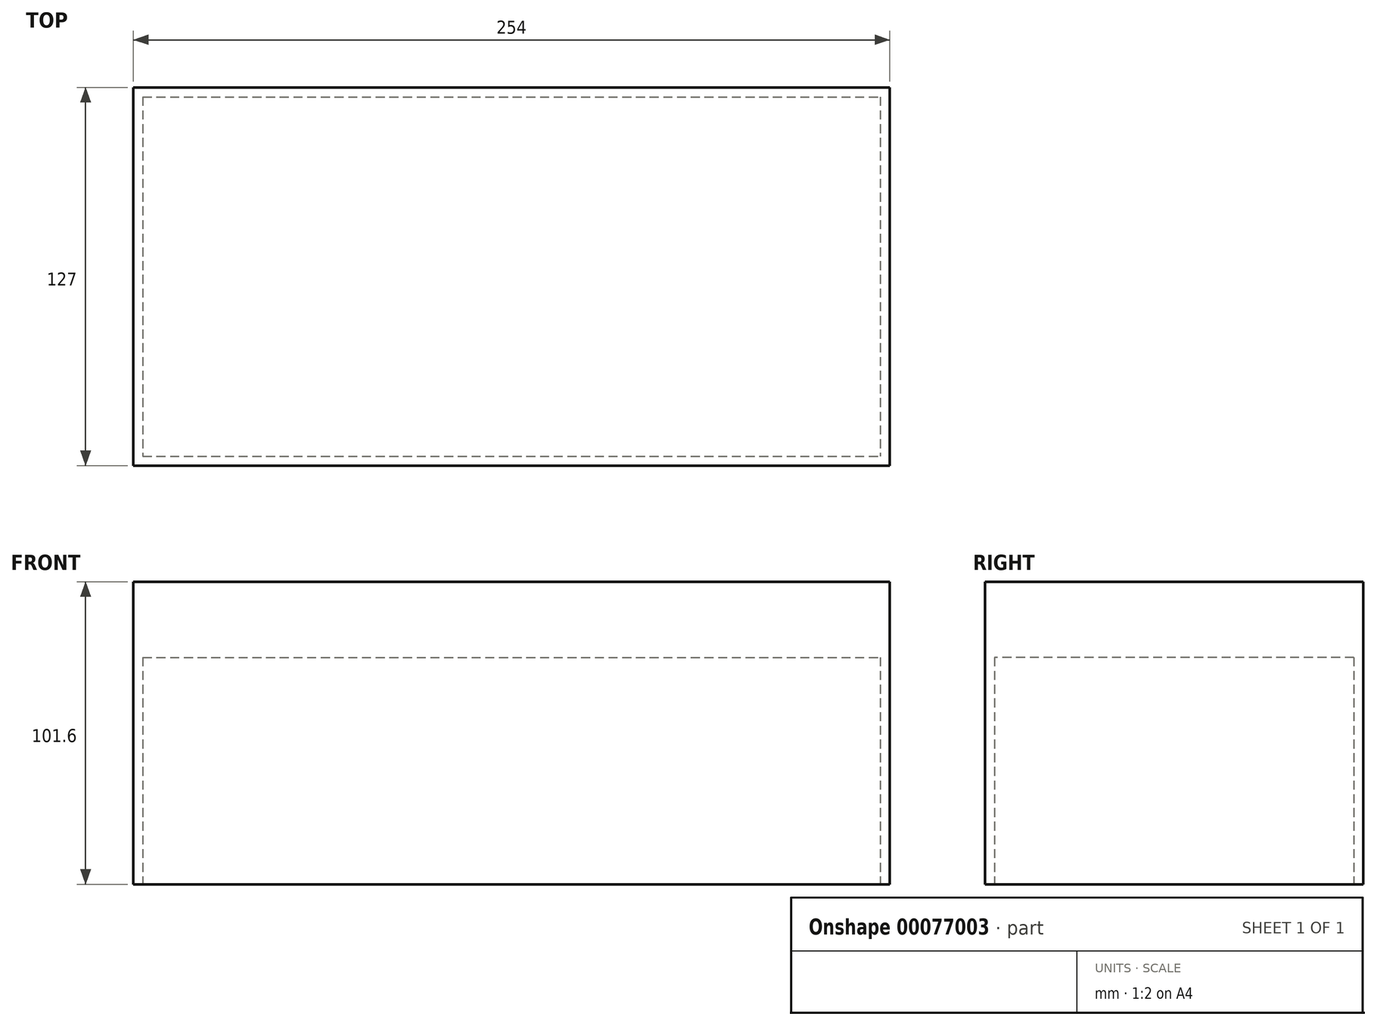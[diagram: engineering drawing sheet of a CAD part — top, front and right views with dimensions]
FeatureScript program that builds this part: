
annotation { "Feature Type Name" : "Feature", "Feature Type Description" : "" }
export const myFeature = defineFeature(function(context is Context, id is Id, definition is map)
    precondition{}
    {
        {
            var Q0;
            Q0=qCreatedBy(makeId("Top.planeOp"),FACE);
            var sketch = newSketch(context, id + "F0", { "sketchPlane" : qUnion([Q0])});
            skLineSegment(sketch, "E0.bottom", {"start": v(-127, 63.5) * mm, "end": v(127, 63.5) * mm});
            skLineSegment(sketch, "E0.top", {"start": v(-127, -63.5) * mm, "end": v(127, -63.5) * mm});
            skLineSegment(sketch, "E0.left", {"start": v(-127, 63.5) * mm, "end": v(-127, -63.5) * mm});
            skLineSegment(sketch, "E0.right", {"start": v(127, 63.5) * mm, "end": v(127, -63.5) * mm});
            skPoint(sketch, "E0.middle", {"position": v(0, 0) * mm});
            skLineSegment(sketch, "E1.bottom", {"start": v(-123.83, 60.33) * mm, "end": v(123.83, 60.33) * mm});
            skLineSegment(sketch, "E1.top", {"start": v(-123.83, -60.33) * mm, "end": v(123.83, -60.33) * mm});
            skLineSegment(sketch, "E1.left", {"start": v(-123.82, 60.33) * mm, "end": v(-123.82, -60.33) * mm});
            skLineSegment(sketch, "E1.right", {"start": v(123.83, 60.33) * mm, "end": v(123.83, -60.33) * mm});
            skSolve(sketch);
        }
        {
            var Q0;
            Q0 = qSketchRegion(id + "F0", true);
            extrude(context, id + "F1", {"entities" : qUnion([Q0]), "depth" : 76.2 * mm});
        }
        {
            var Q0;
            Q0=makeQuery(id+"F1.opExtrude","CAP_FACE",FACE,{"disambiguationData":[OSD([sQuery(id+"F0.wireOp",EDGE,"E0.bottom"),sQuery(id+"F0.wireOp",EDGE,"E0.top"),sQuery(id+"F0.wireOp",EDGE,"E0.left"),sQuery(id+"F0.wireOp",EDGE,"E0.right"),sQuery(id+"F0.wireOp",EDGE,"E1.bottom"),sQuery(id+"F0.wireOp",EDGE,"E1.top"),sQuery(id+"F0.wireOp",EDGE,"E1.left"),sQuery(id+"F0.wireOp",EDGE,"E1.right")])],"isStart":false});
            var sketch = newSketch(context, id + "F2", { "sketchPlane" : qUnion([Q0])});
            skLineSegment(sketch, "E2.bottom", {"start": v(-127, -63.5) * mm, "end": v(127, -63.5) * mm});
            skLineSegment(sketch, "E2.top", {"start": v(-127, 63.5) * mm, "end": v(127, 63.5) * mm});
            skLineSegment(sketch, "E2.left", {"start": v(-127, -63.5) * mm, "end": v(-127, 63.5) * mm});
            skLineSegment(sketch, "E2.right", {"start": v(127, -63.5) * mm, "end": v(127, 63.5) * mm});
            skSolve(sketch);
        }
        {
            var Q0;
            Q0 = qSketchRegion(id + "F2", true);
            extrude(context, id + "F3", {"entities" : qUnion([Q0]), "operationType" : NewBodyOperationType.ADD, "depth" : 25.4 * mm});
        }
    });
